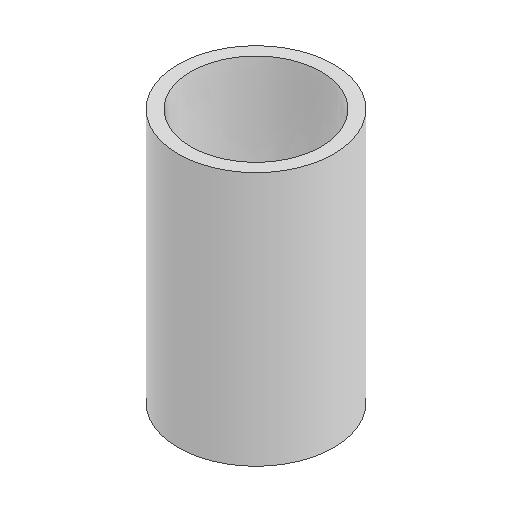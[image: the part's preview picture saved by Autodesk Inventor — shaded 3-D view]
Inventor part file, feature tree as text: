
AUTODESK INVENTOR PART (.ipt)
format: ipt  version: 2023 (Build 270158000, 158)  size: 258,048 bytes
history: native  units: in
note: dims shown in document units (in); Inventor stores cm internally (conversion verified against a paired STEP export)
features: other x1, extrude x1, sketch x1
ambient origin geometry x8: Origin, YZ Plane, XZ Plane, XY Plane, X Axis, Y Axis, Z Axis, Center Point
bodies: Body1 (feature_tree)
feature tree (3):
  other  "Sólido1"
  extrude  "Extrusión1"  Depth=1.378in
  sketch  "Boceto2"  dims[d0=0.7055in d1=0.8425in d2=1.378in d3=0.0in]
